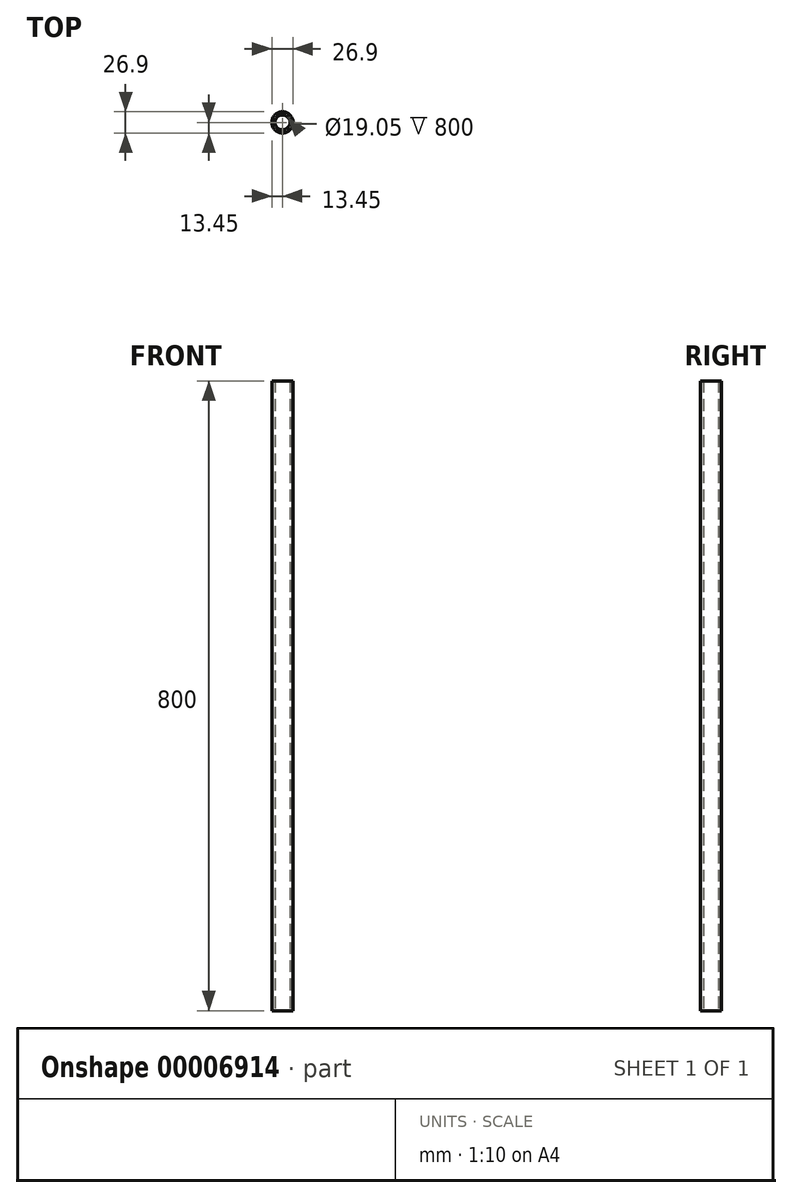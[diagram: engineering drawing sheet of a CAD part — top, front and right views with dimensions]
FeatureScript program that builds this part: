
annotation { "Feature Type Name" : "Feature", "Feature Type Description" : "" }
export const myFeature = defineFeature(function(context is Context, id is Id, definition is map)
    precondition{}
    {
        {
            var Q0;
            Q0=qCreatedBy(makeId("Top.planeOp"),FACE);
            var sketch = newSketch(context, id + "F0", { "sketchPlane" : qUnion([Q0])});
            skCircle(sketch, "E0", {"center": v(0, 0) * mm, "radius": 13.45 * mm});
            skCircle(sketch, "E1", {"center": v(0, 0) * mm, "radius": 9.53 * mm});
            skSolve(sketch);
        }
        {
            var Q0;
            Q0=makeQuery(id+"F0.imprint","IMPRINT",FACE,{"disambiguationData":[TD([[makeQuery(id+"F0.imprint","IMPRINT",EDGE,{"derivedFrom":sQuery(id+"F0.wireOp",EDGE,"E0")}),1.0]])]});
            extrude(context, id + "F1", {"entities" : qUnion([Q0]), "depth" : (800) * mm});
        }
    });
